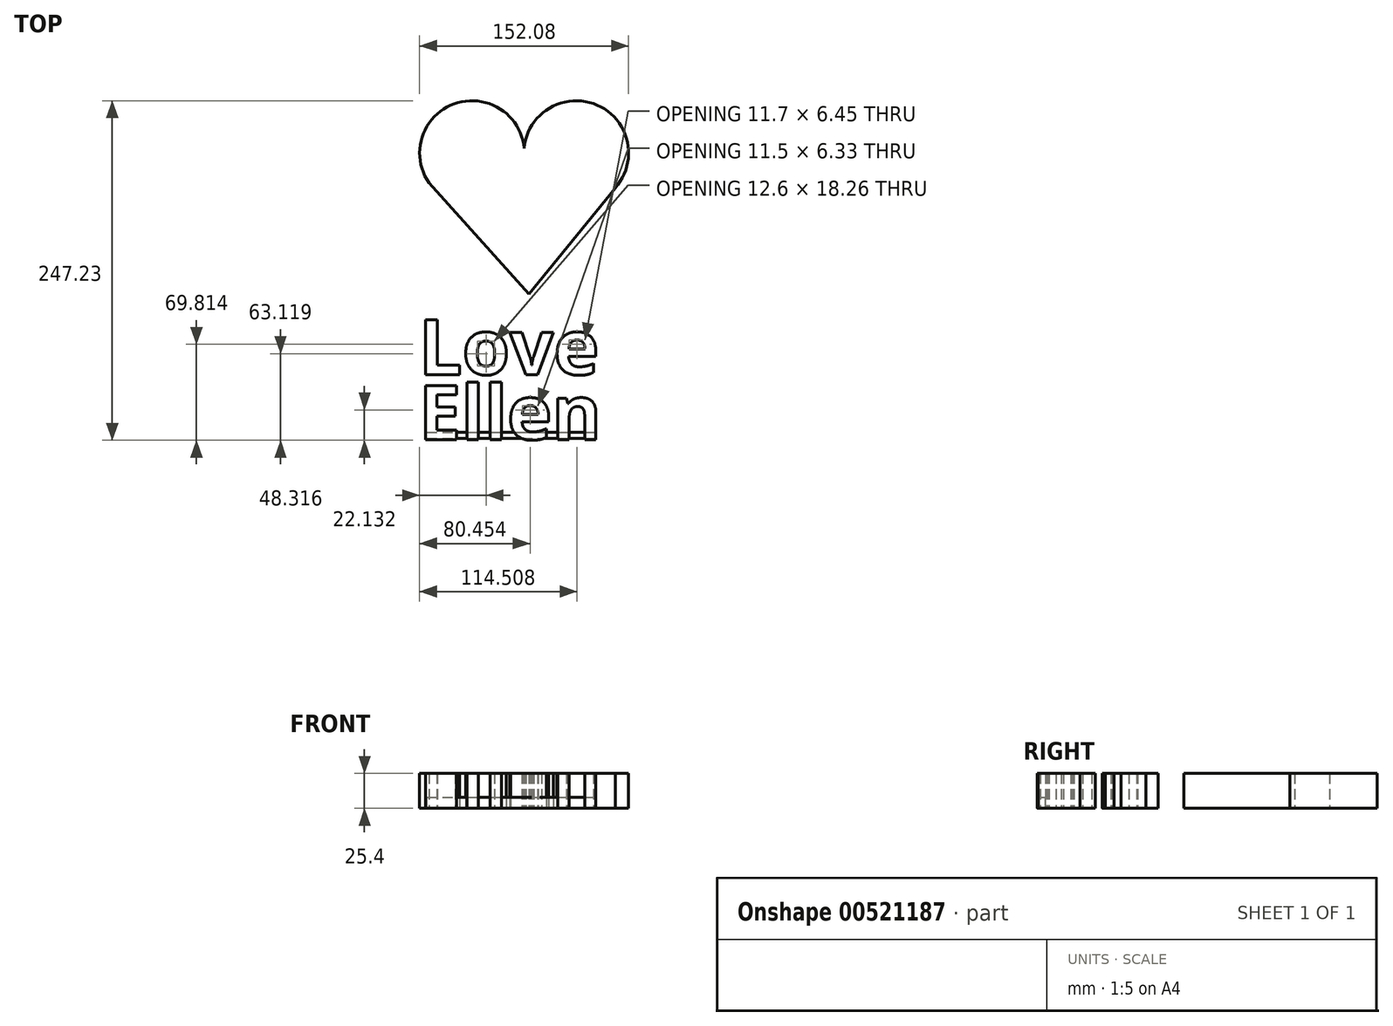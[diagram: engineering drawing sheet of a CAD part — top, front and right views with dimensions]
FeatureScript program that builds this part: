
annotation { "Feature Type Name" : "Feature", "Feature Type Description" : "" }
export const myFeature = defineFeature(function(context is Context, id is Id, definition is map)
    precondition{}
    {
        {
            var Q0;
            Q0=qCreatedBy(makeId("Top.planeOp"),FACE);
            var sketch = newSketch(context, id + "F0", { "sketchPlane" : qUnion([Q0])});
            skText(sketch, "E0", { "text": "Love", "fontName": "OpenSans-Bold.ttf"});
            skText(sketch, "E1", { "text": "Ellen", "fontName": "OpenSans-Bold.ttf"});
            skPoint(sketch, "E1.firstSnap0", {"position": v(-132.42, -20.15) * mm});
            const initialGuessF0  = {"E0": [-0.13242, -0.0403, 1, 0, 0.0403], "E1": [-0.13242, -0.0876, 1, 0, 0.0396]};
            skSetInitialGuess(sketch, initialGuessF0);
            skSolve(sketch);
        }
        {
            var Q0;
            Q0 = qSketchRegion(id + "F0", true);
            extrude(context, id + "F1", {"entities" : qUnion([Q0]), "depth" : 25.4 * mm, "offsetDistance" : 25.4 * mm});
        }
        {
            var Q0;
            Q0=qCreatedBy(makeId("Top.planeOp"),FACE);
            var sketch = newSketch(context, id + "F2", { "sketchPlane" : qUnion([Q0])});
            skCircle(sketch, "E2", {"center": v(-93.7, 120.99) * mm, "radius": 38.1 * mm});
            skCircle(sketch, "E3", {"center": v(-17.82, 120.99) * mm, "radius": 38.1 * mm});
            skLineSegment(sketch, "E4", {"start": v(-125.04, 99.31) * mm, "end": v(-52.3, 18.49) * mm});
            skLineSegment(sketch, "E5", {"start": v(-52.3, 18.49) * mm, "end": v(10.53, 95.54) * mm});
            skLineSegment(sketch, "E6", {"start": v(10.53, 95.54) * mm, "end": v(-42.38, 125) * mm});
            skLineSegment(sketch, "E7", {"start": v(-42.38, 125) * mm, "end": v(-107.45, 117.63) * mm});
            skLineSegment(sketch, "E8", {"start": v(-107.45, 117.63) * mm, "end": v(-125.04, 99.31) * mm});
            skSolve(sketch);
        }
        {
            var Q0;
            {var subQ5=sQuery(id+"F2.wireOp",EDGE,"E6");Q0=makeQuery(id+"F2.imprint","IMPRINT",FACE,{"disambiguationData":[TD([[makeQuery(id+"F2.imprint","IMPRINT",EDGE,{"derivedFrom":subQ5}),1.0]])]});}
            var Q1;
            {var subQ0=sQuery(id+"F2.wireOp",EDGE,"E3");var subQ1=sQuery(id+"F2.wireOp",EDGE,"E2");var subQ2=makeQuery(id+"F2.imprint","INTERSECT",VERTEX,{"disambiguationData":[OD(0.0)],"derivedFrom":[subQ1,subQ0]});Q1=makeQuery(id+"F2.imprint","IMPRINT",FACE,{"disambiguationData":[TD([[makeQuery(id+"F2.imprint","IMPRINT",EDGE,{"disambiguationData":[TD([[subQ2,1.0]])],"derivedFrom":subQ1}),1.0]])]});}
            var Q2;
            {var subQ0=sQuery(id+"F2.wireOp",EDGE,"E7");var subQ1=sQuery(id+"F2.wireOp",EDGE,"E2");var subQ2=makeQuery(id+"F2.imprint","INTERSECT",VERTEX,{"derivedFrom":[subQ1,subQ0]});Q2=makeQuery(id+"F2.imprint","IMPRINT",FACE,{"disambiguationData":[TD([[makeQuery(id+"F2.imprint","IMPRINT",EDGE,{"disambiguationData":[TD([[subQ2,1.0]])],"derivedFrom":subQ1}),1.0]])]});}
            var Q3;
            {var subQ5=sQuery(id+"F2.wireOp",EDGE,"E5");Q3=makeQuery(id+"F2.imprint","IMPRINT",FACE,{"disambiguationData":[TD([[makeQuery(id+"F2.imprint","IMPRINT",EDGE,{"derivedFrom":subQ5}),1.0]])]});}
            var Q4;
            {var subQ0=sQuery(id+"F2.wireOp",EDGE,"E8");Q4=makeQuery(id+"F2.imprint","IMPRINT",FACE,{"disambiguationData":[TD([[makeQuery(id+"F2.imprint","IMPRINT",EDGE,{"derivedFrom":subQ0}),1.0]])]});}
            var Q5;
            {var subQ0=sQuery(id+"F2.wireOp",EDGE,"E8");Q5=makeQuery(id+"F2.imprint","IMPRINT",FACE,{"disambiguationData":[TD([[makeQuery(id+"F2.imprint","IMPRINT",EDGE,{"derivedFrom":subQ0}),-1.0]])]});}
            var Q6;
            {var subQ5=sQuery(id+"F2.wireOp",EDGE,"E6");Q6=makeQuery(id+"F2.imprint","IMPRINT",FACE,{"disambiguationData":[TD([[makeQuery(id+"F2.imprint","IMPRINT",EDGE,{"derivedFrom":subQ5}),-1.0]])]});}
            extrude(context, id + "F3", {"entities" : qUnion([Q0, Q1, Q2, Q3, Q4, Q5, Q6]), "depth" : 25.4 * mm, "offsetDistance" : 25.4 * mm});
        }
        {
            var Q0;
            Q0=qCreatedBy(makeId("Top.planeOp"),FACE);
            var sketch = newSketch(context, id + "F4", { "sketchPlane" : qUnion([Q0])});
            skLineSegment(sketch, "E9.bottom", {"start": v(-126.71, -86.88) * mm, "end": v(-3.7, -86.88) * mm});
            skLineSegment(sketch, "E9.top", {"start": v(-126.71, -82.42) * mm, "end": v(-3.7, -82.42) * mm});
            skLineSegment(sketch, "E9.left", {"start": v(-126.71, -86.88) * mm, "end": v(-126.71, -82.42) * mm});
            skLineSegment(sketch, "E9.right", {"start": v(-3.7, -86.88) * mm, "end": v(-3.7, -82.42) * mm});
            skSolve(sketch);
        }
        {
            var Q0;
            Q0=makeQuery(id+"F4.imprint","IMPRINT",FACE,{"disambiguationData":[TD([[makeQuery(id+"F4.imprint","IMPRINT",EDGE,{"derivedFrom":sQuery(id+"F4.wireOp",EDGE,"E9.bottom")}),1.0]])]});
            extrude(context, id + "F5", {"entities" : qUnion([Q0]), "depth" : 7.87 * mm, "offsetDistance" : 25.4 * mm});
        }
    });
